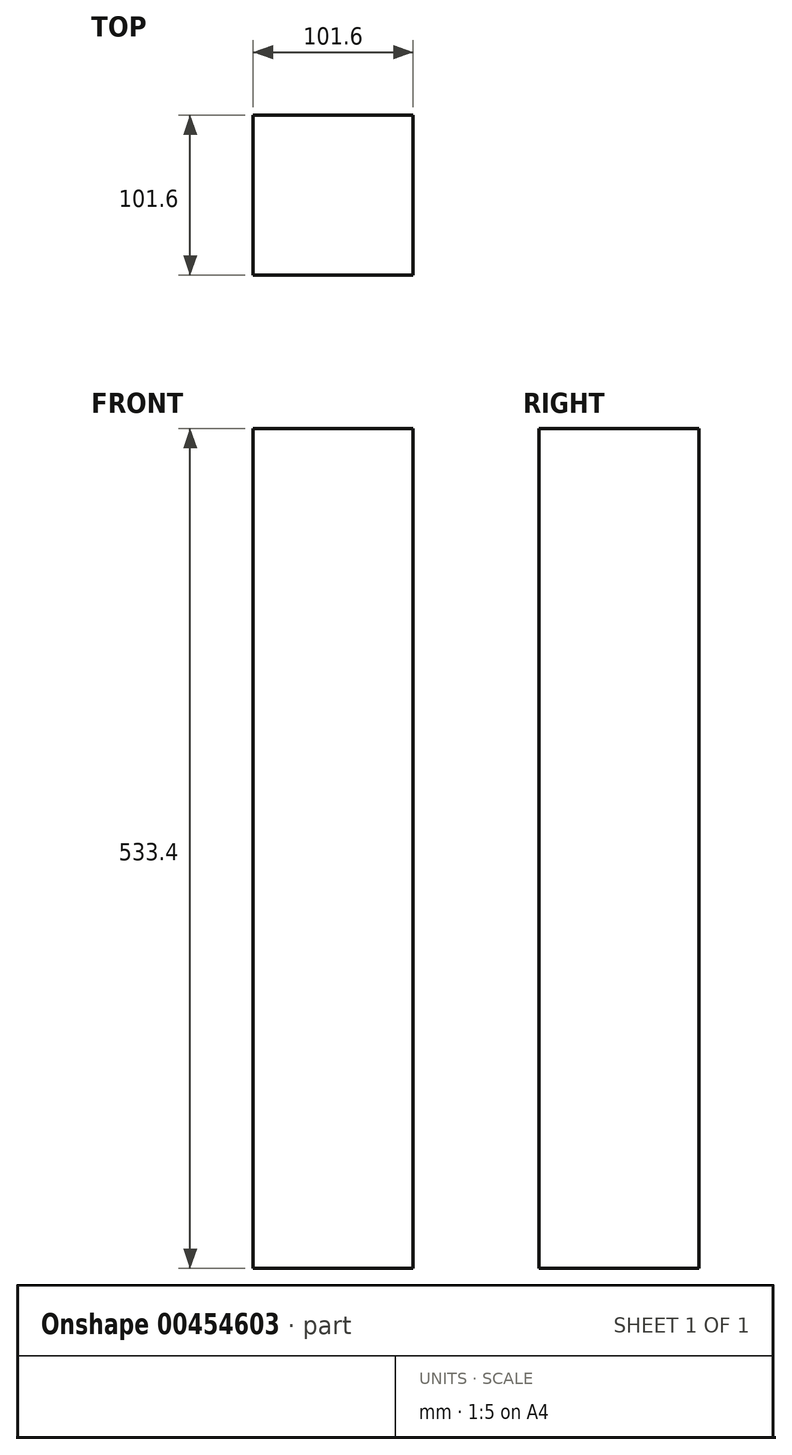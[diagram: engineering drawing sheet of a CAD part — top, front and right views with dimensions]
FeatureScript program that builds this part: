
annotation { "Feature Type Name" : "Feature", "Feature Type Description" : "" }
export const myFeature = defineFeature(function(context is Context, id is Id, definition is map)
    precondition{}
    {
        {
            var Q0;
            Q0=qCreatedBy(makeId("Top.planeOp"),FACE);
            var sketch = newSketch(context, id + "F0", { "sketchPlane" : qUnion([Q0])});
            skLineSegment(sketch, "E0.bottom", {"start": v(50.8, 50.8) * mm, "end": v(-50.8, 50.8) * mm});
            skLineSegment(sketch, "E0.top", {"start": v(50.8, -50.8) * mm, "end": v(-50.8, -50.8) * mm});
            skLineSegment(sketch, "E0.left", {"start": v(50.8, 50.8) * mm, "end": v(50.8, -50.8) * mm});
            skLineSegment(sketch, "E0.right", {"start": v(-50.8, 50.8) * mm, "end": v(-50.8, -50.8) * mm});
            skPoint(sketch, "E0.middle", {"position": v(0, 0) * mm});
            skSolve(sketch);
        }
        {
            var Q0;
            Q0=makeQuery(id+"F0.imprint","IMPRINT",FACE,{"disambiguationData":[TD([[makeQuery(id+"F0.imprint","IMPRINT",EDGE,{"derivedFrom":sQuery(id+"F0.wireOp",EDGE,"E0.bottom")}),1.0]])]});
            extrude(context, id + "F1", {"entities" : qUnion([Q0]), "depth" : 533.4 * mm});
        }
    });
